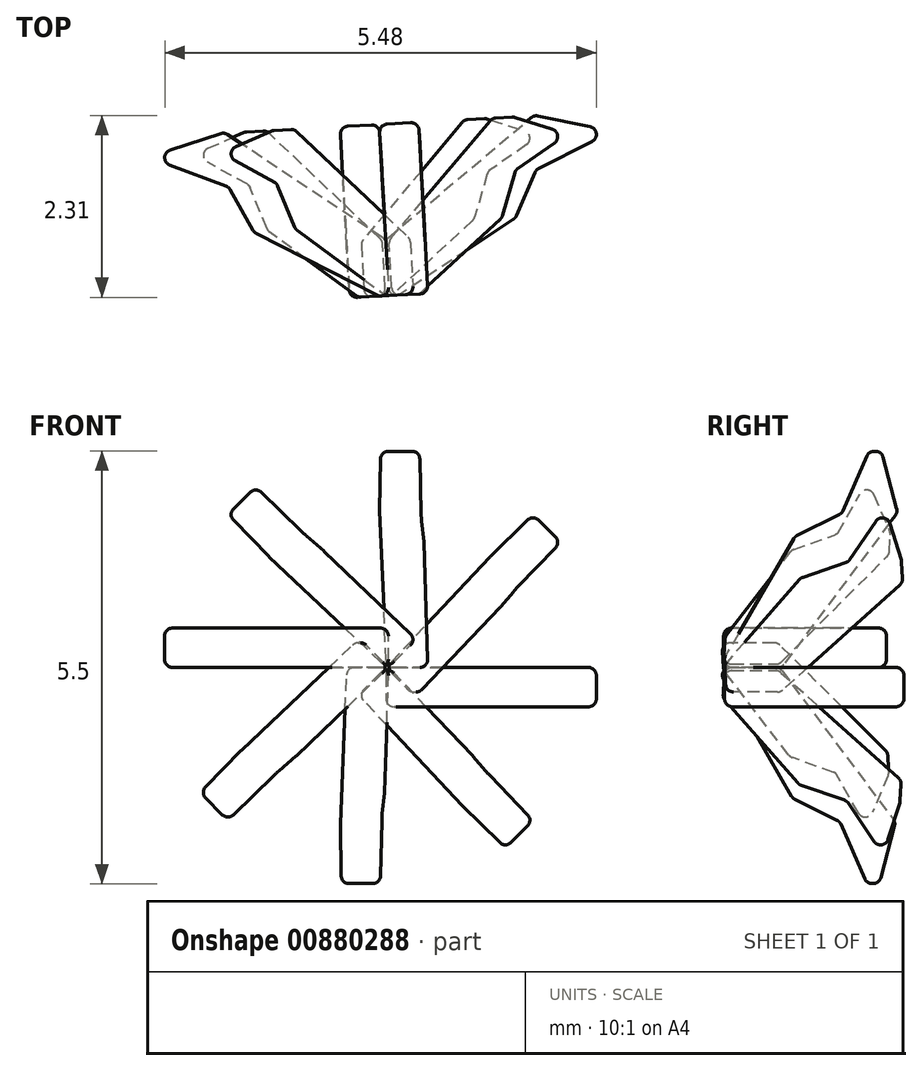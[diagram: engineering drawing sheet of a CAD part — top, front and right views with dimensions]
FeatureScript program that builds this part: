
annotation { "Feature Type Name" : "Feature", "Feature Type Description" : "" }
export const myFeature = defineFeature(function(context is Context, id is Id, definition is map)
    precondition{}
    {
        {
            var Q0;
            Q0=qCreatedBy(makeId("Top.planeOp"),FACE);
            var sketch = newSketch(context, id + "F0", { "sketchPlane" : qUnion([Q0])});
            skLineSegment(sketch, "E0", {"start": v(4.09, 0.78) * mm, "end": v(5.97, 2.37) * mm});
            skLineSegment(sketch, "E1", {"start": v(5.97, 2.37) * mm, "end": v(6.96, 2.16) * mm});
            skLineSegment(sketch, "E2", {"start": v(6.96, 2.16) * mm, "end": v(6, 1.67) * mm});
            skLineSegment(sketch, "E3", {"start": v(6, 1.67) * mm, "end": v(5.73, 1.06) * mm});
            skLineSegment(sketch, "E4", {"start": v(5.73, 1.06) * mm, "end": v(4.13, 0) * mm});
            skLineSegment(sketch, "E5", {"start": v(4.13, 0) * mm, "end": v(4.09, 0.78) * mm});
            skSolve(sketch);
        }
        {
            var Q0;
            Q0=makeQuery(id+"F0.imprint","IMPRINT",FACE,{"disambiguationData":[TD([[makeQuery(id+"F0.imprint","IMPRINT",EDGE,{"derivedFrom":sQuery(id+"F0.wireOp",EDGE,"E0")}),-1.0]])]});
            extrude(context, id + "F1", {"entities" : qUnion([Q0]), "depth" : .5 * mm, "offsetDistance" : 25 * mm});
        }
        {
            var Q0;
            Q0=makeQuery(id+"F1.opExtrude","SWEPT_BODY",BODY,{"disambiguationData":[OSD([sQuery(id+"F0.wireOp",EDGE,"E0"),sQuery(id+"F0.wireOp",EDGE,"E1"),sQuery(id+"F0.wireOp",EDGE,"E2"),sQuery(id+"F0.wireOp",EDGE,"E3"),sQuery(id+"F0.wireOp",EDGE,"E4"),sQuery(id+"F0.wireOp",EDGE,"E5")])]});
            var Q1;
            Q1=makeQuery(id+"F1.opExtrude","CAP_EDGE",EDGE,{"disambiguationData":[OSD([sQuery(id+"F0.wireOp",EDGE,"E5")])],"isStart":false});
            circularPattern(context, id + "F2", {"entities" : qUnion([Q0]), "axis" : qUnion([Q1]), "angle" : 360 * degree, "instanceCount" : 8, "equalSpace" : true});
        }
        {
            var Q0;
            Q0=makeQuery(id+"F2.opPattern","COPY",EDGE,{"derivedFrom":makeQuery(id+"F1.opExtrude","SWEPT_EDGE",EDGE,{"disambiguationData":[OSD([sQuery(id+"F0.wireOp",EDGE,"E0"),sQuery(id+"F0.wireOp",EDGE,"E1")])]}),"instanceName":"4"});
            var Q1;
            Q1=makeQuery(id+"F2.opPattern","COPY",EDGE,{"derivedFrom":makeQuery(id+"F1.opExtrude","CAP_EDGE",EDGE,{"disambiguationData":[OSD([sQuery(id+"F0.wireOp",EDGE,"E0")])],"isStart":false}),"instanceName":"4"});
            var Q2;
            Q2=makeQuery(id+"F2.opPattern","COPY",FACE,{"derivedFrom":makeQuery(id+"F1.opExtrude","SWEPT_FACE",FACE,{"disambiguationData":[OSD([sQuery(id+"F0.wireOp",EDGE,"E0")])]}),"instanceName":"4"});
            var Q3;
            Q3=makeQuery(id+"F2.opPattern","COPY",FACE,{"derivedFrom":makeQuery(id+"F1.opExtrude","CAP_FACE",FACE,{"disambiguationData":[OSD([sQuery(id+"F0.wireOp",EDGE,"E0"),sQuery(id+"F0.wireOp",EDGE,"E1"),sQuery(id+"F0.wireOp",EDGE,"E2"),sQuery(id+"F0.wireOp",EDGE,"E3"),sQuery(id+"F0.wireOp",EDGE,"E4"),sQuery(id+"F0.wireOp",EDGE,"E5")])],"isStart":false}),"instanceName":"4"});
            var Q4;
            Q4=makeQuery(id+"F2.opPattern","COPY",EDGE,{"derivedFrom":makeQuery(id+"F1.opExtrude","CAP_EDGE",EDGE,{"disambiguationData":[OSD([sQuery(id+"F0.wireOp",EDGE,"E0")])],"isStart":true}),"instanceName":"4"});
            var Q5;
            Q5=makeQuery(id+"F2.opPattern","COPY",FACE,{"derivedFrom":makeQuery(id+"F1.opExtrude","CAP_FACE",FACE,{"disambiguationData":[OSD([sQuery(id+"F0.wireOp",EDGE,"E0"),sQuery(id+"F0.wireOp",EDGE,"E1"),sQuery(id+"F0.wireOp",EDGE,"E2"),sQuery(id+"F0.wireOp",EDGE,"E3"),sQuery(id+"F0.wireOp",EDGE,"E4"),sQuery(id+"F0.wireOp",EDGE,"E5")])],"isStart":true}),"instanceName":"4"});
            var Q6;
            Q6=makeQuery(id+"F2.opPattern","COPY",FACE,{"derivedFrom":makeQuery(id+"F1.opExtrude","SWEPT_FACE",FACE,{"disambiguationData":[OSD([sQuery(id+"F0.wireOp",EDGE,"E2")])]}),"instanceName":"4"});
            var Q7;
            Q7=makeQuery(id+"F2.opPattern","COPY",FACE,{"derivedFrom":makeQuery(id+"F1.opExtrude","SWEPT_FACE",FACE,{"disambiguationData":[OSD([sQuery(id+"F0.wireOp",EDGE,"E1")])]}),"instanceName":"4"});
            var Q8;
            Q8=makeQuery(id+"F2.opPattern","COPY",FACE,{"derivedFrom":makeQuery(id+"F1.opExtrude","CAP_FACE",FACE,{"disambiguationData":[OSD([sQuery(id+"F0.wireOp",EDGE,"E0"),sQuery(id+"F0.wireOp",EDGE,"E1"),sQuery(id+"F0.wireOp",EDGE,"E2"),sQuery(id+"F0.wireOp",EDGE,"E3"),sQuery(id+"F0.wireOp",EDGE,"E4"),sQuery(id+"F0.wireOp",EDGE,"E5")])],"isStart":false}),"instanceName":"5"});
            var Q9;
            Q9=makeQuery(id+"F2.opPattern","COPY",EDGE,{"derivedFrom":makeQuery(id+"F1.opExtrude","CAP_EDGE",EDGE,{"disambiguationData":[OSD([sQuery(id+"F0.wireOp",EDGE,"E0")])],"isStart":true}),"instanceName":"5"});
            var Q10;
            Q10=makeQuery(id+"F2.opPattern","COPY",FACE,{"derivedFrom":makeQuery(id+"F1.opExtrude","SWEPT_FACE",FACE,{"disambiguationData":[OSD([sQuery(id+"F0.wireOp",EDGE,"E1")])]}),"instanceName":"5"});
            var Q11;
            Q11=makeQuery(id+"F2.opPattern","COPY",FACE,{"derivedFrom":makeQuery(id+"F1.opExtrude","SWEPT_FACE",FACE,{"disambiguationData":[OSD([sQuery(id+"F0.wireOp",EDGE,"E2")])]}),"instanceName":"5"});
            var Q12;
            Q12=makeQuery(id+"F2.opPattern","COPY",FACE,{"derivedFrom":makeQuery(id+"F1.opExtrude","SWEPT_FACE",FACE,{"disambiguationData":[OSD([sQuery(id+"F0.wireOp",EDGE,"E0")])]}),"instanceName":"5"});
            var Q13;
            Q13=makeQuery(id+"F2.opPattern","COPY",FACE,{"derivedFrom":makeQuery(id+"F1.opExtrude","CAP_FACE",FACE,{"disambiguationData":[OSD([sQuery(id+"F0.wireOp",EDGE,"E0"),sQuery(id+"F0.wireOp",EDGE,"E1"),sQuery(id+"F0.wireOp",EDGE,"E2"),sQuery(id+"F0.wireOp",EDGE,"E3"),sQuery(id+"F0.wireOp",EDGE,"E4"),sQuery(id+"F0.wireOp",EDGE,"E5")])],"isStart":true}),"instanceName":"5"});
            var Q14;
            Q14=makeQuery(id+"F2.opPattern","COPY",FACE,{"derivedFrom":makeQuery(id+"F1.opExtrude","SWEPT_FACE",FACE,{"disambiguationData":[OSD([sQuery(id+"F0.wireOp",EDGE,"E3")])]}),"instanceName":"5"});
            var Q15;
            Q15=makeQuery(id+"F2.opPattern","COPY",FACE,{"derivedFrom":makeQuery(id+"F1.opExtrude","CAP_FACE",FACE,{"disambiguationData":[OSD([sQuery(id+"F0.wireOp",EDGE,"E0"),sQuery(id+"F0.wireOp",EDGE,"E1"),sQuery(id+"F0.wireOp",EDGE,"E2"),sQuery(id+"F0.wireOp",EDGE,"E3"),sQuery(id+"F0.wireOp",EDGE,"E4"),sQuery(id+"F0.wireOp",EDGE,"E5")])],"isStart":false}),"instanceName":"3"});
            var Q16;
            Q16=makeQuery(id+"F2.opPattern","COPY",FACE,{"derivedFrom":makeQuery(id+"F1.opExtrude","SWEPT_FACE",FACE,{"disambiguationData":[OSD([sQuery(id+"F0.wireOp",EDGE,"E2")])]}),"instanceName":"3"});
            var Q17;
            Q17=makeQuery(id+"F2.opPattern","COPY",FACE,{"derivedFrom":makeQuery(id+"F1.opExtrude","SWEPT_FACE",FACE,{"disambiguationData":[OSD([sQuery(id+"F0.wireOp",EDGE,"E0")])]}),"instanceName":"3"});
            var Q18;
            Q18=makeQuery(id+"F2.opPattern","COPY",EDGE,{"derivedFrom":makeQuery(id+"F1.opExtrude","CAP_EDGE",EDGE,{"disambiguationData":[OSD([sQuery(id+"F0.wireOp",EDGE,"E1")])],"isStart":false}),"instanceName":"3"});
            var Q19;
            Q19=makeQuery(id+"F2.opPattern","COPY",FACE,{"derivedFrom":makeQuery(id+"F1.opExtrude","SWEPT_FACE",FACE,{"disambiguationData":[OSD([sQuery(id+"F0.wireOp",EDGE,"E1")])]}),"instanceName":"3"});
            var Q20;
            Q20=makeQuery(id+"F2.opPattern","COPY",FACE,{"derivedFrom":makeQuery(id+"F1.opExtrude","CAP_FACE",FACE,{"disambiguationData":[OSD([sQuery(id+"F0.wireOp",EDGE,"E0"),sQuery(id+"F0.wireOp",EDGE,"E1"),sQuery(id+"F0.wireOp",EDGE,"E2"),sQuery(id+"F0.wireOp",EDGE,"E3"),sQuery(id+"F0.wireOp",EDGE,"E4"),sQuery(id+"F0.wireOp",EDGE,"E5")])],"isStart":true}),"instanceName":"3"});
            var Q21;
            Q21=makeQuery(id+"F2.opPattern","COPY",EDGE,{"derivedFrom":makeQuery(id+"F1.opExtrude","CAP_EDGE",EDGE,{"disambiguationData":[OSD([sQuery(id+"F0.wireOp",EDGE,"E0")])],"isStart":true}),"instanceName":"7"});
            var Q22;
            Q22=makeQuery(id+"F2.opPattern","COPY",EDGE,{"derivedFrom":makeQuery(id+"F1.opExtrude","SWEPT_EDGE",EDGE,{"disambiguationData":[OSD([sQuery(id+"F0.wireOp",EDGE,"E1"),sQuery(id+"F0.wireOp",EDGE,"E2")])]}),"instanceName":"7"});
            var Q23;
            Q23=makeQuery(id+"F2.opPattern","COPY",FACE,{"derivedFrom":makeQuery(id+"F1.opExtrude","CAP_FACE",FACE,{"disambiguationData":[OSD([sQuery(id+"F0.wireOp",EDGE,"E0"),sQuery(id+"F0.wireOp",EDGE,"E1"),sQuery(id+"F0.wireOp",EDGE,"E2"),sQuery(id+"F0.wireOp",EDGE,"E3"),sQuery(id+"F0.wireOp",EDGE,"E4"),sQuery(id+"F0.wireOp",EDGE,"E5")])],"isStart":false}),"instanceName":"7"});
            var Q24;
            Q24=makeQuery(id+"F2.opPattern","COPY",FACE,{"derivedFrom":makeQuery(id+"F1.opExtrude","SWEPT_FACE",FACE,{"disambiguationData":[OSD([sQuery(id+"F0.wireOp",EDGE,"E0")])]}),"instanceName":"7"});
            var Q25;
            Q25=makeQuery(id+"F2.opPattern","COPY",EDGE,{"derivedFrom":makeQuery(id+"F1.opExtrude","CAP_EDGE",EDGE,{"disambiguationData":[OSD([sQuery(id+"F0.wireOp",EDGE,"E0")])],"isStart":false}),"instanceName":"7"});
            var Q26;
            Q26=makeQuery(id+"F2.opPattern","COPY",FACE,{"derivedFrom":makeQuery(id+"F1.opExtrude","SWEPT_FACE",FACE,{"disambiguationData":[OSD([sQuery(id+"F0.wireOp",EDGE,"E1")])]}),"instanceName":"7"});
            var Q27;
            Q27=makeQuery(id+"F2.opPattern","COPY",FACE,{"derivedFrom":makeQuery(id+"F1.opExtrude","CAP_FACE",FACE,{"disambiguationData":[OSD([sQuery(id+"F0.wireOp",EDGE,"E0"),sQuery(id+"F0.wireOp",EDGE,"E1"),sQuery(id+"F0.wireOp",EDGE,"E2"),sQuery(id+"F0.wireOp",EDGE,"E3"),sQuery(id+"F0.wireOp",EDGE,"E4"),sQuery(id+"F0.wireOp",EDGE,"E5")])],"isStart":true}),"instanceName":"7"});
            var Q28;
            Q28=makeQuery(id+"F2.opPattern","COPY",FACE,{"derivedFrom":makeQuery(id+"F1.opExtrude","SWEPT_FACE",FACE,{"disambiguationData":[OSD([sQuery(id+"F0.wireOp",EDGE,"E3")])]}),"instanceName":"7"});
            var Q29;
            Q29=makeQuery(id+"F2.opPattern","COPY",FACE,{"derivedFrom":makeQuery(id+"F1.opExtrude","SWEPT_FACE",FACE,{"disambiguationData":[OSD([sQuery(id+"F0.wireOp",EDGE,"E0")])]}),"instanceName":"6"});
            var Q30;
            Q30=makeQuery(id+"F2.opPattern","COPY",EDGE,{"derivedFrom":makeQuery(id+"F1.opExtrude","SWEPT_EDGE",EDGE,{"disambiguationData":[OSD([sQuery(id+"F0.wireOp",EDGE,"E0"),sQuery(id+"F0.wireOp",EDGE,"E1")])]}),"instanceName":"6"});
            var Q31;
            Q31=makeQuery(id+"F2.opPattern","COPY",FACE,{"derivedFrom":makeQuery(id+"F1.opExtrude","SWEPT_FACE",FACE,{"disambiguationData":[OSD([sQuery(id+"F0.wireOp",EDGE,"E5")])]}),"instanceName":"6"});
            var Q32;
            Q32=makeQuery(id+"F2.opPattern","COPY",FACE,{"derivedFrom":makeQuery(id+"F1.opExtrude","CAP_FACE",FACE,{"disambiguationData":[OSD([sQuery(id+"F0.wireOp",EDGE,"E0"),sQuery(id+"F0.wireOp",EDGE,"E1"),sQuery(id+"F0.wireOp",EDGE,"E2"),sQuery(id+"F0.wireOp",EDGE,"E3"),sQuery(id+"F0.wireOp",EDGE,"E4"),sQuery(id+"F0.wireOp",EDGE,"E5")])],"isStart":true}),"instanceName":"6"});
            var Q33;
            Q33=makeQuery(id+"F2.opPattern","COPY",FACE,{"derivedFrom":makeQuery(id+"F1.opExtrude","CAP_FACE",FACE,{"disambiguationData":[OSD([sQuery(id+"F0.wireOp",EDGE,"E0"),sQuery(id+"F0.wireOp",EDGE,"E1"),sQuery(id+"F0.wireOp",EDGE,"E2"),sQuery(id+"F0.wireOp",EDGE,"E3"),sQuery(id+"F0.wireOp",EDGE,"E4"),sQuery(id+"F0.wireOp",EDGE,"E5")])],"isStart":false}),"instanceName":"6"});
            var Q34;
            Q34=makeQuery(id+"F2.opPattern","COPY",EDGE,{"derivedFrom":makeQuery(id+"F1.opExtrude","CAP_EDGE",EDGE,{"disambiguationData":[OSD([sQuery(id+"F0.wireOp",EDGE,"E0")])],"isStart":false}),"instanceName":"6"});
            var Q35;
            Q35=makeQuery(id+"F2.opPattern","COPY",FACE,{"derivedFrom":makeQuery(id+"F1.opExtrude","SWEPT_FACE",FACE,{"disambiguationData":[OSD([sQuery(id+"F0.wireOp",EDGE,"E1")])]}),"instanceName":"6"});
            var Q36;
            Q36=makeQuery(id+"F1.opExtrude","CAP_FACE",FACE,{"disambiguationData":[OSD([sQuery(id+"F0.wireOp",EDGE,"E0"),sQuery(id+"F0.wireOp",EDGE,"E1"),sQuery(id+"F0.wireOp",EDGE,"E2"),sQuery(id+"F0.wireOp",EDGE,"E3"),sQuery(id+"F0.wireOp",EDGE,"E4"),sQuery(id+"F0.wireOp",EDGE,"E5")])],"isStart":true});
            var Q37;
            Q37=makeQuery(id+"F1.opExtrude","CAP_EDGE",EDGE,{"disambiguationData":[OSD([sQuery(id+"F0.wireOp",EDGE,"E1")])],"isStart":false});
            var Q38;
            Q38=makeQuery(id+"F1.opExtrude","SWEPT_EDGE",EDGE,{"disambiguationData":[OSD([sQuery(id+"F0.wireOp",EDGE,"E0"),sQuery(id+"F0.wireOp",EDGE,"E1")])]});
            var Q39;
            Q39=makeQuery(id+"F1.opExtrude","SWEPT_FACE",FACE,{"disambiguationData":[OSD([sQuery(id+"F0.wireOp",EDGE,"E0")])]});
            var Q40;
            Q40=makeQuery(id+"F1.opExtrude","SWEPT_FACE",FACE,{"disambiguationData":[OSD([sQuery(id+"F0.wireOp",EDGE,"E1")])]});
            var Q41;
            Q41=makeQuery(id+"F2.opPattern","COPY",FACE,{"derivedFrom":makeQuery(id+"F1.opExtrude","CAP_FACE",FACE,{"disambiguationData":[OSD([sQuery(id+"F0.wireOp",EDGE,"E0"),sQuery(id+"F0.wireOp",EDGE,"E1"),sQuery(id+"F0.wireOp",EDGE,"E2"),sQuery(id+"F0.wireOp",EDGE,"E3"),sQuery(id+"F0.wireOp",EDGE,"E4"),sQuery(id+"F0.wireOp",EDGE,"E5")])],"isStart":false}),"instanceName":"2"});
            var Q42;
            Q42=makeQuery(id+"F2.opPattern","COPY",FACE,{"derivedFrom":makeQuery(id+"F1.opExtrude","SWEPT_FACE",FACE,{"disambiguationData":[OSD([sQuery(id+"F0.wireOp",EDGE,"E1")])]}),"instanceName":"2"});
            var Q43;
            Q43=makeQuery(id+"F2.opPattern","COPY",FACE,{"derivedFrom":makeQuery(id+"F1.opExtrude","SWEPT_FACE",FACE,{"disambiguationData":[OSD([sQuery(id+"F0.wireOp",EDGE,"E0")])]}),"instanceName":"2"});
            var Q44;
            Q44=makeQuery(id+"F2.opPattern","COPY",FACE,{"derivedFrom":makeQuery(id+"F1.opExtrude","CAP_FACE",FACE,{"disambiguationData":[OSD([sQuery(id+"F0.wireOp",EDGE,"E0"),sQuery(id+"F0.wireOp",EDGE,"E1"),sQuery(id+"F0.wireOp",EDGE,"E2"),sQuery(id+"F0.wireOp",EDGE,"E3"),sQuery(id+"F0.wireOp",EDGE,"E4"),sQuery(id+"F0.wireOp",EDGE,"E5")])],"isStart":true}),"instanceName":"2"});
            var Q45;
            Q45=makeQuery(id+"F2.opPattern","COPY",EDGE,{"derivedFrom":makeQuery(id+"F1.opExtrude","CAP_EDGE",EDGE,{"disambiguationData":[OSD([sQuery(id+"F0.wireOp",EDGE,"E0")])],"isStart":true}),"instanceName":"1"});
            var Q46;
            Q46=makeQuery(id+"F2.opPattern","COPY",FACE,{"derivedFrom":makeQuery(id+"F1.opExtrude","CAP_FACE",FACE,{"disambiguationData":[OSD([sQuery(id+"F0.wireOp",EDGE,"E0"),sQuery(id+"F0.wireOp",EDGE,"E1"),sQuery(id+"F0.wireOp",EDGE,"E2"),sQuery(id+"F0.wireOp",EDGE,"E3"),sQuery(id+"F0.wireOp",EDGE,"E4"),sQuery(id+"F0.wireOp",EDGE,"E5")])],"isStart":true}),"instanceName":"1"});
            var Q47;
            Q47=makeQuery(id+"F2.opPattern","COPY",EDGE,{"derivedFrom":makeQuery(id+"F1.opExtrude","CAP_EDGE",EDGE,{"disambiguationData":[OSD([sQuery(id+"F0.wireOp",EDGE,"E1")])],"isStart":true}),"instanceName":"1"});
            var Q48;
            Q48=makeQuery(id+"F2.opPattern","COPY",FACE,{"derivedFrom":makeQuery(id+"F1.opExtrude","SWEPT_FACE",FACE,{"disambiguationData":[OSD([sQuery(id+"F0.wireOp",EDGE,"E0")])]}),"instanceName":"1"});
            var Q49;
            Q49=makeQuery(id+"F2.opPattern","COPY",EDGE,{"derivedFrom":makeQuery(id+"F1.opExtrude","CAP_EDGE",EDGE,{"disambiguationData":[OSD([sQuery(id+"F0.wireOp",EDGE,"E0")])],"isStart":false}),"instanceName":"1"});
            var Q50;
            Q50=makeQuery(id+"F2.opPattern","COPY",EDGE,{"derivedFrom":makeQuery(id+"F1.opExtrude","CAP_EDGE",EDGE,{"disambiguationData":[OSD([sQuery(id+"F0.wireOp",EDGE,"E1")])],"isStart":false}),"instanceName":"1"});
            var Q51;
            Q51=makeQuery(id+"F2.opPattern","COPY",FACE,{"derivedFrom":makeQuery(id+"F1.opExtrude","SWEPT_FACE",FACE,{"disambiguationData":[OSD([sQuery(id+"F0.wireOp",EDGE,"E1")])]}),"instanceName":"1"});
            var Q52;
            Q52=makeQuery(id+"F2.opPattern","COPY",EDGE,{"derivedFrom":makeQuery(id+"F1.opExtrude","SWEPT_EDGE",EDGE,{"disambiguationData":[OSD([sQuery(id+"F0.wireOp",EDGE,"E2"),sQuery(id+"F0.wireOp",EDGE,"E3")])]}),"instanceName":"4"});
            var Q53;
            Q53=makeQuery(id+"F2.opPattern","COPY",EDGE,{"derivedFrom":makeQuery(id+"F1.opExtrude","SWEPT_EDGE",EDGE,{"disambiguationData":[OSD([sQuery(id+"F0.wireOp",EDGE,"E1"),sQuery(id+"F0.wireOp",EDGE,"E2")])]}),"instanceName":"4"});
            var Q54;
            Q54=makeQuery(id+"F2.opPattern","COPY",FACE,{"derivedFrom":makeQuery(id+"F1.opExtrude","SWEPT_FACE",FACE,{"disambiguationData":[OSD([sQuery(id+"F0.wireOp",EDGE,"E3")])]}),"instanceName":"4"});
            var Q55;
            Q55=makeQuery(id+"F2.opPattern","COPY",EDGE,{"derivedFrom":makeQuery(id+"F1.opExtrude","CAP_EDGE",EDGE,{"disambiguationData":[OSD([sQuery(id+"F0.wireOp",EDGE,"E3")])],"isStart":false}),"instanceName":"4"});
            var Q56;
            Q56=makeQuery(id+"F2.opPattern","COPY",EDGE,{"derivedFrom":makeQuery(id+"F1.opExtrude","CAP_EDGE",EDGE,{"disambiguationData":[OSD([sQuery(id+"F0.wireOp",EDGE,"E1")])],"isStart":false}),"instanceName":"4"});
            var Q57;
            Q57=makeQuery(id+"F2.opPattern","COPY",EDGE,{"derivedFrom":makeQuery(id+"F1.opExtrude","CAP_EDGE",EDGE,{"disambiguationData":[OSD([sQuery(id+"F0.wireOp",EDGE,"E2")])],"isStart":false}),"instanceName":"4"});
            var Q58;
            Q58=makeQuery(id+"F2.opPattern","COPY",FACE,{"derivedFrom":makeQuery(id+"F1.opExtrude","SWEPT_FACE",FACE,{"disambiguationData":[OSD([sQuery(id+"F0.wireOp",EDGE,"E4")])]}),"instanceName":"4"});
            var Q59;
            Q59=makeQuery(id+"F2.opPattern","COPY",EDGE,{"derivedFrom":makeQuery(id+"F1.opExtrude","CAP_EDGE",EDGE,{"disambiguationData":[OSD([sQuery(id+"F0.wireOp",EDGE,"E1")])],"isStart":true}),"instanceName":"4"});
            var Q60;
            Q60=makeQuery(id+"F2.opPattern","COPY",EDGE,{"derivedFrom":makeQuery(id+"F1.opExtrude","CAP_EDGE",EDGE,{"disambiguationData":[OSD([sQuery(id+"F0.wireOp",EDGE,"E2")])],"isStart":true}),"instanceName":"4"});
            var Q61;
            Q61=makeQuery(id+"F2.opPattern","COPY",EDGE,{"derivedFrom":makeQuery(id+"F1.opExtrude","SWEPT_EDGE",EDGE,{"disambiguationData":[OSD([sQuery(id+"F0.wireOp",EDGE,"E2"),sQuery(id+"F0.wireOp",EDGE,"E3")])]}),"instanceName":"5"});
            var Q62;
            Q62=makeQuery(id+"F2.opPattern","COPY",EDGE,{"derivedFrom":makeQuery(id+"F1.opExtrude","CAP_EDGE",EDGE,{"disambiguationData":[OSD([sQuery(id+"F0.wireOp",EDGE,"E1")])],"isStart":true}),"instanceName":"5"});
            var Q63;
            Q63=makeQuery(id+"F2.opPattern","COPY",EDGE,{"derivedFrom":makeQuery(id+"F1.opExtrude","SWEPT_EDGE",EDGE,{"disambiguationData":[OSD([sQuery(id+"F0.wireOp",EDGE,"E0"),sQuery(id+"F0.wireOp",EDGE,"E1")])]}),"instanceName":"5"});
            var Q64;
            Q64=makeQuery(id+"F2.opPattern","COPY",EDGE,{"derivedFrom":makeQuery(id+"F1.opExtrude","CAP_EDGE",EDGE,{"disambiguationData":[OSD([sQuery(id+"F0.wireOp",EDGE,"E2")])],"isStart":false}),"instanceName":"5"});
            var Q65;
            Q65=makeQuery(id+"F2.opPattern","COPY",EDGE,{"derivedFrom":makeQuery(id+"F1.opExtrude","CAP_EDGE",EDGE,{"disambiguationData":[OSD([sQuery(id+"F0.wireOp",EDGE,"E3")])],"isStart":false}),"instanceName":"5"});
            var Q66;
            Q66=makeQuery(id+"F2.opPattern","COPY",EDGE,{"derivedFrom":makeQuery(id+"F1.opExtrude","SWEPT_EDGE",EDGE,{"disambiguationData":[OSD([sQuery(id+"F0.wireOp",EDGE,"E3"),sQuery(id+"F0.wireOp",EDGE,"E4")])]}),"instanceName":"5"});
            var Q67;
            Q67=makeQuery(id+"F2.opPattern","COPY",FACE,{"derivedFrom":makeQuery(id+"F1.opExtrude","SWEPT_FACE",FACE,{"disambiguationData":[OSD([sQuery(id+"F0.wireOp",EDGE,"E4")])]}),"instanceName":"5"});
            var Q68;
            Q68=makeQuery(id+"F2.opPattern","COPY",EDGE,{"derivedFrom":makeQuery(id+"F1.opExtrude","CAP_EDGE",EDGE,{"disambiguationData":[OSD([sQuery(id+"F0.wireOp",EDGE,"E3")])],"isStart":true}),"instanceName":"5"});
            var Q69;
            Q69=makeQuery(id+"F2.opPattern","COPY",EDGE,{"derivedFrom":makeQuery(id+"F1.opExtrude","SWEPT_EDGE",EDGE,{"disambiguationData":[OSD([sQuery(id+"F0.wireOp",EDGE,"E1"),sQuery(id+"F0.wireOp",EDGE,"E2")])]}),"instanceName":"5"});
            var Q70;
            Q70=makeQuery(id+"F2.opPattern","COPY",EDGE,{"derivedFrom":makeQuery(id+"F1.opExtrude","CAP_EDGE",EDGE,{"disambiguationData":[OSD([sQuery(id+"F0.wireOp",EDGE,"E0")])],"isStart":false}),"instanceName":"5"});
            var Q71;
            Q71=makeQuery(id+"F2.opPattern","COPY",EDGE,{"derivedFrom":makeQuery(id+"F1.opExtrude","CAP_EDGE",EDGE,{"disambiguationData":[OSD([sQuery(id+"F0.wireOp",EDGE,"E1")])],"isStart":false}),"instanceName":"5"});
            var Q72;
            Q72=makeQuery(id+"F2.opPattern","COPY",EDGE,{"derivedFrom":makeQuery(id+"F1.opExtrude","CAP_EDGE",EDGE,{"disambiguationData":[OSD([sQuery(id+"F0.wireOp",EDGE,"E2")])],"isStart":true}),"instanceName":"5"});
            var Q73;
            Q73=makeQuery(id+"F2.opPattern","COPY",EDGE,{"derivedFrom":makeQuery(id+"F1.opExtrude","CAP_EDGE",EDGE,{"disambiguationData":[OSD([sQuery(id+"F0.wireOp",EDGE,"E1")])],"isStart":true}),"instanceName":"3"});
            var Q74;
            Q74=makeQuery(id+"F2.opPattern","COPY",EDGE,{"derivedFrom":makeQuery(id+"F1.opExtrude","SWEPT_EDGE",EDGE,{"disambiguationData":[OSD([sQuery(id+"F0.wireOp",EDGE,"E3"),sQuery(id+"F0.wireOp",EDGE,"E4")])]}),"instanceName":"3"});
            var Q75;
            Q75=makeQuery(id+"F2.opPattern","COPY",FACE,{"derivedFrom":makeQuery(id+"F1.opExtrude","SWEPT_FACE",FACE,{"disambiguationData":[OSD([sQuery(id+"F0.wireOp",EDGE,"E3")])]}),"instanceName":"3"});
            var Q76;
            Q76=makeQuery(id+"F2.opPattern","COPY",EDGE,{"derivedFrom":makeQuery(id+"F1.opExtrude","CAP_EDGE",EDGE,{"disambiguationData":[OSD([sQuery(id+"F0.wireOp",EDGE,"E2")])],"isStart":true}),"instanceName":"3"});
            var Q77;
            Q77=makeQuery(id+"F2.opPattern","COPY",EDGE,{"derivedFrom":makeQuery(id+"F1.opExtrude","CAP_EDGE",EDGE,{"disambiguationData":[OSD([sQuery(id+"F0.wireOp",EDGE,"E0")])],"isStart":true}),"instanceName":"3"});
            var Q78;
            Q78=makeQuery(id+"F2.opPattern","COPY",EDGE,{"derivedFrom":makeQuery(id+"F1.opExtrude","CAP_EDGE",EDGE,{"disambiguationData":[OSD([sQuery(id+"F0.wireOp",EDGE,"E0")])],"isStart":false}),"instanceName":"3"});
            var Q79;
            Q79=makeQuery(id+"F2.opPattern","COPY",EDGE,{"derivedFrom":makeQuery(id+"F1.opExtrude","SWEPT_EDGE",EDGE,{"disambiguationData":[OSD([sQuery(id+"F0.wireOp",EDGE,"E1"),sQuery(id+"F0.wireOp",EDGE,"E2")])]}),"instanceName":"3"});
            var Q80;
            Q80=makeQuery(id+"F2.opPattern","COPY",EDGE,{"derivedFrom":makeQuery(id+"F1.opExtrude","SWEPT_EDGE",EDGE,{"disambiguationData":[OSD([sQuery(id+"F0.wireOp",EDGE,"E2"),sQuery(id+"F0.wireOp",EDGE,"E3")])]}),"instanceName":"3"});
            var Q81;
            Q81=makeQuery(id+"F2.opPattern","COPY",EDGE,{"derivedFrom":makeQuery(id+"F1.opExtrude","CAP_EDGE",EDGE,{"disambiguationData":[OSD([sQuery(id+"F0.wireOp",EDGE,"E2")])],"isStart":false}),"instanceName":"3"});
            var Q82;
            Q82=makeQuery(id+"F2.opPattern","COPY",FACE,{"derivedFrom":makeQuery(id+"F1.opExtrude","SWEPT_FACE",FACE,{"disambiguationData":[OSD([sQuery(id+"F0.wireOp",EDGE,"E4")])]}),"instanceName":"3"});
            var Q83;
            Q83=makeQuery(id+"F2.opPattern","COPY",EDGE,{"derivedFrom":makeQuery(id+"F1.opExtrude","SWEPT_EDGE",EDGE,{"disambiguationData":[OSD([sQuery(id+"F0.wireOp",EDGE,"E0"),sQuery(id+"F0.wireOp",EDGE,"E1")])]}),"instanceName":"3"});
            var Q84;
            Q84=makeQuery(id+"F2.opPattern","COPY",EDGE,{"derivedFrom":makeQuery(id+"F1.opExtrude","CAP_EDGE",EDGE,{"disambiguationData":[OSD([sQuery(id+"F0.wireOp",EDGE,"E3")])],"isStart":true}),"instanceName":"7"});
            var Q85;
            Q85=makeQuery(id+"F2.opPattern","COPY",FACE,{"derivedFrom":makeQuery(id+"F1.opExtrude","SWEPT_FACE",FACE,{"disambiguationData":[OSD([sQuery(id+"F0.wireOp",EDGE,"E4")])]}),"instanceName":"7"});
            var Q86;
            Q86=makeQuery(id+"F2.opPattern","COPY",EDGE,{"derivedFrom":makeQuery(id+"F1.opExtrude","CAP_EDGE",EDGE,{"disambiguationData":[OSD([sQuery(id+"F0.wireOp",EDGE,"E3")])],"isStart":false}),"instanceName":"7"});
            var Q87;
            Q87=makeQuery(id+"F2.opPattern","COPY",EDGE,{"derivedFrom":makeQuery(id+"F1.opExtrude","SWEPT_EDGE",EDGE,{"disambiguationData":[OSD([sQuery(id+"F0.wireOp",EDGE,"E2"),sQuery(id+"F0.wireOp",EDGE,"E3")])]}),"instanceName":"7"});
            var Q88;
            Q88=makeQuery(id+"F2.opPattern","COPY",EDGE,{"derivedFrom":makeQuery(id+"F1.opExtrude","CAP_EDGE",EDGE,{"disambiguationData":[OSD([sQuery(id+"F0.wireOp",EDGE,"E1")])],"isStart":true}),"instanceName":"7"});
            var Q89;
            Q89=makeQuery(id+"F2.opPattern","COPY",EDGE,{"derivedFrom":makeQuery(id+"F1.opExtrude","CAP_EDGE",EDGE,{"disambiguationData":[OSD([sQuery(id+"F0.wireOp",EDGE,"E1")])],"isStart":false}),"instanceName":"7"});
            var Q90;
            Q90=makeQuery(id+"F2.opPattern","COPY",FACE,{"derivedFrom":makeQuery(id+"F1.opExtrude","SWEPT_FACE",FACE,{"disambiguationData":[OSD([sQuery(id+"F0.wireOp",EDGE,"E2")])]}),"instanceName":"7"});
            var Q91;
            Q91=makeQuery(id+"F2.opPattern","COPY",EDGE,{"derivedFrom":makeQuery(id+"F1.opExtrude","SWEPT_EDGE",EDGE,{"disambiguationData":[OSD([sQuery(id+"F0.wireOp",EDGE,"E0"),sQuery(id+"F0.wireOp",EDGE,"E1")])]}),"instanceName":"7"});
            var Q92;
            Q92=makeQuery(id+"F2.opPattern","COPY",EDGE,{"derivedFrom":makeQuery(id+"F1.opExtrude","SWEPT_EDGE",EDGE,{"disambiguationData":[OSD([sQuery(id+"F0.wireOp",EDGE,"E3"),sQuery(id+"F0.wireOp",EDGE,"E4")])]}),"instanceName":"7"});
            var Q93;
            Q93=makeQuery(id+"F2.opPattern","COPY",EDGE,{"derivedFrom":makeQuery(id+"F1.opExtrude","CAP_EDGE",EDGE,{"disambiguationData":[OSD([sQuery(id+"F0.wireOp",EDGE,"E2")])],"isStart":true}),"instanceName":"7"});
            var Q94;
            Q94=makeQuery(id+"F2.opPattern","COPY",EDGE,{"derivedFrom":makeQuery(id+"F1.opExtrude","CAP_EDGE",EDGE,{"disambiguationData":[OSD([sQuery(id+"F0.wireOp",EDGE,"E4")])],"isStart":false}),"instanceName":"7"});
            var Q95;
            Q95=makeQuery(id+"F2.opPattern","COPY",EDGE,{"derivedFrom":makeQuery(id+"F1.opExtrude","CAP_EDGE",EDGE,{"disambiguationData":[OSD([sQuery(id+"F0.wireOp",EDGE,"E4")])],"isStart":true}),"instanceName":"7"});
            var Q96;
            Q96=makeQuery(id+"F2.opPattern","COPY",EDGE,{"derivedFrom":makeQuery(id+"F1.opExtrude","SWEPT_EDGE",EDGE,{"disambiguationData":[OSD([sQuery(id+"F0.wireOp",EDGE,"E3"),sQuery(id+"F0.wireOp",EDGE,"E4")])]}),"instanceName":"6"});
            var Q97;
            Q97=makeQuery(id+"F2.opPattern","COPY",FACE,{"derivedFrom":makeQuery(id+"F1.opExtrude","SWEPT_FACE",FACE,{"disambiguationData":[OSD([sQuery(id+"F0.wireOp",EDGE,"E3")])]}),"instanceName":"6"});
            var Q98;
            Q98=makeQuery(id+"F2.opPattern","COPY",FACE,{"derivedFrom":makeQuery(id+"F1.opExtrude","SWEPT_FACE",FACE,{"disambiguationData":[OSD([sQuery(id+"F0.wireOp",EDGE,"E4")])]}),"instanceName":"6"});
            var Q99;
            Q99=makeQuery(id+"F2.opPattern","COPY",EDGE,{"derivedFrom":makeQuery(id+"F1.opExtrude","CAP_EDGE",EDGE,{"disambiguationData":[OSD([sQuery(id+"F0.wireOp",EDGE,"E0")])],"isStart":true}),"instanceName":"6"});
            var Q100;
            Q100=makeQuery(id+"F2.opPattern","COPY",EDGE,{"derivedFrom":makeQuery(id+"F1.opExtrude","SWEPT_EDGE",EDGE,{"disambiguationData":[OSD([sQuery(id+"F0.wireOp",EDGE,"E1"),sQuery(id+"F0.wireOp",EDGE,"E2")])]}),"instanceName":"6"});
            var Q101;
            Q101=makeQuery(id+"F2.opPattern","COPY",EDGE,{"derivedFrom":makeQuery(id+"F1.opExtrude","CAP_EDGE",EDGE,{"disambiguationData":[OSD([sQuery(id+"F0.wireOp",EDGE,"E1")])],"isStart":false}),"instanceName":"6"});
            var Q102;
            Q102=makeQuery(id+"F2.opPattern","COPY",EDGE,{"derivedFrom":makeQuery(id+"F1.opExtrude","CAP_EDGE",EDGE,{"disambiguationData":[OSD([sQuery(id+"F0.wireOp",EDGE,"E1")])],"isStart":true}),"instanceName":"6"});
            var Q103;
            Q103=makeQuery(id+"F2.opPattern","COPY",EDGE,{"derivedFrom":makeQuery(id+"F1.opExtrude","SWEPT_EDGE",EDGE,{"disambiguationData":[OSD([sQuery(id+"F0.wireOp",EDGE,"E2"),sQuery(id+"F0.wireOp",EDGE,"E3")])]}),"instanceName":"6"});
            var Q104;
            Q104=makeQuery(id+"F2.opPattern","COPY",FACE,{"derivedFrom":makeQuery(id+"F1.opExtrude","SWEPT_FACE",FACE,{"disambiguationData":[OSD([sQuery(id+"F0.wireOp",EDGE,"E2")])]}),"instanceName":"6"});
            var Q105;
            Q105=makeQuery(id+"F1.opExtrude","CAP_EDGE",EDGE,{"disambiguationData":[OSD([sQuery(id+"F0.wireOp",EDGE,"E0")])],"isStart":true});
            var Q106;
            Q106=makeQuery(id+"F1.opExtrude","SWEPT_FACE",FACE,{"disambiguationData":[OSD([sQuery(id+"F0.wireOp",EDGE,"E2")])]});
            var Q107;
            Q107=makeQuery(id+"F1.opExtrude","SWEPT_FACE",FACE,{"disambiguationData":[OSD([sQuery(id+"F0.wireOp",EDGE,"E4")])]});
            var Q108;
            Q108=makeQuery(id+"F1.opExtrude","SWEPT_EDGE",EDGE,{"disambiguationData":[OSD([sQuery(id+"F0.wireOp",EDGE,"E2"),sQuery(id+"F0.wireOp",EDGE,"E3")])]});
            var Q109;
            Q109=makeQuery(id+"F1.opExtrude","SWEPT_FACE",FACE,{"disambiguationData":[OSD([sQuery(id+"F0.wireOp",EDGE,"E3")])]});
            var Q110;
            Q110=makeQuery(id+"F1.opExtrude","SWEPT_EDGE",EDGE,{"disambiguationData":[OSD([sQuery(id+"F0.wireOp",EDGE,"E3"),sQuery(id+"F0.wireOp",EDGE,"E4")])]});
            var Q111;
            Q111=makeQuery(id+"F1.opExtrude","SWEPT_EDGE",EDGE,{"disambiguationData":[OSD([sQuery(id+"F0.wireOp",EDGE,"E1"),sQuery(id+"F0.wireOp",EDGE,"E2")])]});
            var Q112;
            Q112=makeQuery(id+"F1.opExtrude","CAP_EDGE",EDGE,{"disambiguationData":[OSD([sQuery(id+"F0.wireOp",EDGE,"E0")])],"isStart":false});
            var Q113;
            Q113=makeQuery(id+"F1.opExtrude","CAP_FACE",FACE,{"disambiguationData":[OSD([sQuery(id+"F0.wireOp",EDGE,"E0"),sQuery(id+"F0.wireOp",EDGE,"E1"),sQuery(id+"F0.wireOp",EDGE,"E2"),sQuery(id+"F0.wireOp",EDGE,"E3"),sQuery(id+"F0.wireOp",EDGE,"E4"),sQuery(id+"F0.wireOp",EDGE,"E5")])],"isStart":false});
            var Q114;
            Q114=makeQuery(id+"F1.opExtrude","CAP_EDGE",EDGE,{"disambiguationData":[OSD([sQuery(id+"F0.wireOp",EDGE,"E1")])],"isStart":true});
            var Q115;
            Q115=makeQuery(id+"F2.opPattern","COPY",EDGE,{"derivedFrom":makeQuery(id+"F1.opExtrude","CAP_EDGE",EDGE,{"disambiguationData":[OSD([sQuery(id+"F0.wireOp",EDGE,"E0")])],"isStart":true}),"instanceName":"2"});
            var Q116;
            Q116=makeQuery(id+"F2.opPattern","COPY",FACE,{"derivedFrom":makeQuery(id+"F1.opExtrude","SWEPT_FACE",FACE,{"disambiguationData":[OSD([sQuery(id+"F0.wireOp",EDGE,"E5")])]}),"instanceName":"2"});
            var Q117;
            Q117=makeQuery(id+"F2.opPattern","COPY",EDGE,{"derivedFrom":makeQuery(id+"F1.opExtrude","SWEPT_EDGE",EDGE,{"disambiguationData":[OSD([sQuery(id+"F0.wireOp",EDGE,"E2"),sQuery(id+"F0.wireOp",EDGE,"E3")])]}),"instanceName":"2"});
            var Q118;
            Q118=makeQuery(id+"F2.opPattern","COPY",FACE,{"derivedFrom":makeQuery(id+"F1.opExtrude","SWEPT_FACE",FACE,{"disambiguationData":[OSD([sQuery(id+"F0.wireOp",EDGE,"E2")])]}),"instanceName":"2"});
            var Q119;
            Q119=makeQuery(id+"F2.opPattern","COPY",EDGE,{"derivedFrom":makeQuery(id+"F1.opExtrude","CAP_EDGE",EDGE,{"disambiguationData":[OSD([sQuery(id+"F0.wireOp",EDGE,"E1")])],"isStart":true}),"instanceName":"2"});
            var Q120;
            Q120=makeQuery(id+"F2.opPattern","COPY",EDGE,{"derivedFrom":makeQuery(id+"F1.opExtrude","CAP_EDGE",EDGE,{"disambiguationData":[OSD([sQuery(id+"F0.wireOp",EDGE,"E1")])],"isStart":false}),"instanceName":"2"});
            var Q121;
            Q121=makeQuery(id+"F2.opPattern","COPY",EDGE,{"derivedFrom":makeQuery(id+"F1.opExtrude","CAP_EDGE",EDGE,{"disambiguationData":[OSD([sQuery(id+"F0.wireOp",EDGE,"E0")])],"isStart":false}),"instanceName":"2"});
            var Q122;
            Q122=makeQuery(id+"F2.opPattern","COPY",FACE,{"derivedFrom":makeQuery(id+"F1.opExtrude","SWEPT_FACE",FACE,{"disambiguationData":[OSD([sQuery(id+"F0.wireOp",EDGE,"E4")])]}),"instanceName":"2"});
            var Q123;
            Q123=makeQuery(id+"F2.opPattern","COPY",EDGE,{"derivedFrom":makeQuery(id+"F1.opExtrude","SWEPT_EDGE",EDGE,{"disambiguationData":[OSD([sQuery(id+"F0.wireOp",EDGE,"E1"),sQuery(id+"F0.wireOp",EDGE,"E2")])]}),"instanceName":"2"});
            var Q124;
            Q124=makeQuery(id+"F2.opPattern","COPY",EDGE,{"derivedFrom":makeQuery(id+"F1.opExtrude","SWEPT_EDGE",EDGE,{"disambiguationData":[OSD([sQuery(id+"F0.wireOp",EDGE,"E0"),sQuery(id+"F0.wireOp",EDGE,"E1")])]}),"instanceName":"2"});
            var Q125;
            Q125=makeQuery(id+"F2.opPattern","COPY",FACE,{"derivedFrom":makeQuery(id+"F1.opExtrude","SWEPT_FACE",FACE,{"disambiguationData":[OSD([sQuery(id+"F0.wireOp",EDGE,"E4")])]}),"instanceName":"1"});
            var Q126;
            Q126=makeQuery(id+"F2.opPattern","COPY",EDGE,{"derivedFrom":makeQuery(id+"F1.opExtrude","SWEPT_EDGE",EDGE,{"disambiguationData":[OSD([sQuery(id+"F0.wireOp",EDGE,"E2"),sQuery(id+"F0.wireOp",EDGE,"E3")])]}),"instanceName":"1"});
            var Q127;
            Q127=makeQuery(id+"F2.opPattern","COPY",EDGE,{"derivedFrom":makeQuery(id+"F1.opExtrude","SWEPT_EDGE",EDGE,{"disambiguationData":[OSD([sQuery(id+"F0.wireOp",EDGE,"E0"),sQuery(id+"F0.wireOp",EDGE,"E5")])]}),"instanceName":"1"});
            var Q128;
            Q128=makeQuery(id+"F2.opPattern","COPY",EDGE,{"derivedFrom":makeQuery(id+"F1.opExtrude","SWEPT_EDGE",EDGE,{"disambiguationData":[OSD([sQuery(id+"F0.wireOp",EDGE,"E0"),sQuery(id+"F0.wireOp",EDGE,"E1")])]}),"instanceName":"1"});
            var Q129;
            Q129=makeQuery(id+"F2.opPattern","COPY",EDGE,{"derivedFrom":makeQuery(id+"F1.opExtrude","SWEPT_EDGE",EDGE,{"disambiguationData":[OSD([sQuery(id+"F0.wireOp",EDGE,"E1"),sQuery(id+"F0.wireOp",EDGE,"E2")])]}),"instanceName":"1"});
            var Q130;
            Q130=makeQuery(id+"F2.opPattern","COPY",FACE,{"derivedFrom":makeQuery(id+"F1.opExtrude","SWEPT_FACE",FACE,{"disambiguationData":[OSD([sQuery(id+"F0.wireOp",EDGE,"E2")])]}),"instanceName":"1"});
            var Q131;
            Q131=makeQuery(id+"F2.opPattern","COPY",FACE,{"derivedFrom":makeQuery(id+"F1.opExtrude","SWEPT_FACE",FACE,{"disambiguationData":[OSD([sQuery(id+"F0.wireOp",EDGE,"E3")])]}),"instanceName":"1"});
            var Q132;
            Q132=makeQuery(id+"F2.opPattern","COPY",EDGE,{"derivedFrom":makeQuery(id+"F1.opExtrude","SWEPT_EDGE",EDGE,{"disambiguationData":[OSD([sQuery(id+"F0.wireOp",EDGE,"E3"),sQuery(id+"F0.wireOp",EDGE,"E4")])]}),"instanceName":"1"});
            var Q133;
            Q133=makeQuery(id+"F2.opPattern","COPY",FACE,{"derivedFrom":makeQuery(id+"F1.opExtrude","SWEPT_FACE",FACE,{"disambiguationData":[OSD([sQuery(id+"F0.wireOp",EDGE,"E5")])]}),"instanceName":"1"});
            var Q134;
            Q134=makeQuery(id+"F2.opPattern","COPY",FACE,{"derivedFrom":makeQuery(id+"F1.opExtrude","CAP_FACE",FACE,{"disambiguationData":[OSD([sQuery(id+"F0.wireOp",EDGE,"E0"),sQuery(id+"F0.wireOp",EDGE,"E1"),sQuery(id+"F0.wireOp",EDGE,"E2"),sQuery(id+"F0.wireOp",EDGE,"E3"),sQuery(id+"F0.wireOp",EDGE,"E4"),sQuery(id+"F0.wireOp",EDGE,"E5")])],"isStart":false}),"instanceName":"1"});
            var Q135;
            Q135=makeQuery(id+"F2.opPattern","COPY",FACE,{"derivedFrom":makeQuery(id+"F1.opExtrude","SWEPT_FACE",FACE,{"disambiguationData":[OSD([sQuery(id+"F0.wireOp",EDGE,"E5")])]}),"instanceName":"4"});
            var Q136;
            Q136=makeQuery(id+"F2.opPattern","COPY",EDGE,{"derivedFrom":makeQuery(id+"F1.opExtrude","SWEPT_EDGE",EDGE,{"disambiguationData":[OSD([sQuery(id+"F0.wireOp",EDGE,"E0"),sQuery(id+"F0.wireOp",EDGE,"E5")])]}),"instanceName":"4"});
            var Q137;
            Q137=makeQuery(id+"F2.opPattern","COPY",EDGE,{"derivedFrom":makeQuery(id+"F1.opExtrude","CAP_EDGE",EDGE,{"disambiguationData":[OSD([sQuery(id+"F0.wireOp",EDGE,"E3")])],"isStart":true}),"instanceName":"4"});
            var Q138;
            Q138=makeQuery(id+"F2.opPattern","COPY",EDGE,{"derivedFrom":makeQuery(id+"F1.opExtrude","CAP_EDGE",EDGE,{"disambiguationData":[OSD([sQuery(id+"F0.wireOp",EDGE,"E4")])],"isStart":true}),"instanceName":"4"});
            var Q139;
            Q139=makeQuery(id+"F2.opPattern","COPY",EDGE,{"derivedFrom":makeQuery(id+"F1.opExtrude","SWEPT_EDGE",EDGE,{"disambiguationData":[OSD([sQuery(id+"F0.wireOp",EDGE,"E3"),sQuery(id+"F0.wireOp",EDGE,"E4")])]}),"instanceName":"4"});
            var Q140;
            Q140=makeQuery(id+"F2.opPattern","COPY",EDGE,{"derivedFrom":makeQuery(id+"F1.opExtrude","CAP_EDGE",EDGE,{"disambiguationData":[OSD([sQuery(id+"F0.wireOp",EDGE,"E4")])],"isStart":false}),"instanceName":"4"});
            var Q141;
            Q141=makeQuery(id+"F2.opPattern","COPY",EDGE,{"derivedFrom":makeQuery(id+"F1.opExtrude","CAP_EDGE",EDGE,{"disambiguationData":[OSD([sQuery(id+"F0.wireOp",EDGE,"E4")])],"isStart":false}),"instanceName":"5"});
            var Q142;
            Q142=makeQuery(id+"F2.opPattern","COPY",FACE,{"derivedFrom":makeQuery(id+"F1.opExtrude","SWEPT_FACE",FACE,{"disambiguationData":[OSD([sQuery(id+"F0.wireOp",EDGE,"E5")])]}),"instanceName":"5"});
            var Q143;
            Q143=makeQuery(id+"F2.opPattern","COPY",EDGE,{"derivedFrom":makeQuery(id+"F1.opExtrude","CAP_EDGE",EDGE,{"disambiguationData":[OSD([sQuery(id+"F0.wireOp",EDGE,"E4")])],"isStart":true}),"instanceName":"5"});
            var Q144;
            Q144=makeQuery(id+"F2.opPattern","COPY",EDGE,{"derivedFrom":makeQuery(id+"F1.opExtrude","CAP_EDGE",EDGE,{"disambiguationData":[OSD([sQuery(id+"F0.wireOp",EDGE,"E4")])],"isStart":true}),"instanceName":"3"});
            var Q145;
            Q145=makeQuery(id+"F2.opPattern","COPY",EDGE,{"derivedFrom":makeQuery(id+"F1.opExtrude","CAP_EDGE",EDGE,{"disambiguationData":[OSD([sQuery(id+"F0.wireOp",EDGE,"E3")])],"isStart":false}),"instanceName":"3"});
            var Q146;
            Q146=makeQuery(id+"F2.opPattern","COPY",EDGE,{"derivedFrom":makeQuery(id+"F1.opExtrude","CAP_EDGE",EDGE,{"disambiguationData":[OSD([sQuery(id+"F0.wireOp",EDGE,"E3")])],"isStart":true}),"instanceName":"3"});
            var Q147;
            Q147=makeQuery(id+"F2.opPattern","COPY",EDGE,{"derivedFrom":makeQuery(id+"F1.opExtrude","CAP_EDGE",EDGE,{"disambiguationData":[OSD([sQuery(id+"F0.wireOp",EDGE,"E4")])],"isStart":false}),"instanceName":"3"});
            var Q148;
            Q148=makeQuery(id+"F2.opPattern","COPY",FACE,{"derivedFrom":makeQuery(id+"F1.opExtrude","SWEPT_FACE",FACE,{"disambiguationData":[OSD([sQuery(id+"F0.wireOp",EDGE,"E5")])]}),"instanceName":"3"});
            var Q149;
            Q149=makeQuery(id+"F2.opPattern","COPY",EDGE,{"derivedFrom":makeQuery(id+"F1.opExtrude","CAP_EDGE",EDGE,{"disambiguationData":[OSD([sQuery(id+"F0.wireOp",EDGE,"E2")])],"isStart":false}),"instanceName":"7"});
            var Q150;
            Q150=makeQuery(id+"F2.opPattern","COPY",FACE,{"derivedFrom":makeQuery(id+"F1.opExtrude","SWEPT_FACE",FACE,{"disambiguationData":[OSD([sQuery(id+"F0.wireOp",EDGE,"E5")])]}),"instanceName":"7"});
            var Q151;
            Q151=makeQuery(id+"F2.opPattern","COPY",EDGE,{"derivedFrom":makeQuery(id+"F1.opExtrude","SWEPT_EDGE",EDGE,{"disambiguationData":[OSD([sQuery(id+"F0.wireOp",EDGE,"E0"),sQuery(id+"F0.wireOp",EDGE,"E5")])]}),"instanceName":"7"});
            var Q152;
            Q152=makeQuery(id+"F2.opPattern","COPY",EDGE,{"derivedFrom":makeQuery(id+"F1.opExtrude","CAP_EDGE",EDGE,{"disambiguationData":[OSD([sQuery(id+"F0.wireOp",EDGE,"E3")])],"isStart":false}),"instanceName":"6"});
            var Q153;
            Q153=makeQuery(id+"F2.opPattern","COPY",EDGE,{"derivedFrom":makeQuery(id+"F1.opExtrude","CAP_EDGE",EDGE,{"disambiguationData":[OSD([sQuery(id+"F0.wireOp",EDGE,"E2")])],"isStart":true}),"instanceName":"6"});
            var Q154;
            Q154=makeQuery(id+"F2.opPattern","COPY",EDGE,{"derivedFrom":makeQuery(id+"F1.opExtrude","CAP_EDGE",EDGE,{"disambiguationData":[OSD([sQuery(id+"F0.wireOp",EDGE,"E4")])],"isStart":false}),"instanceName":"6"});
            var Q155;
            Q155=makeQuery(id+"F2.opPattern","COPY",EDGE,{"derivedFrom":makeQuery(id+"F1.opExtrude","CAP_EDGE",EDGE,{"disambiguationData":[OSD([sQuery(id+"F0.wireOp",EDGE,"E2")])],"isStart":false}),"instanceName":"6"});
            var Q156;
            Q156=makeQuery(id+"F2.opPattern","COPY",EDGE,{"derivedFrom":makeQuery(id+"F1.opExtrude","CAP_EDGE",EDGE,{"disambiguationData":[OSD([sQuery(id+"F0.wireOp",EDGE,"E3")])],"isStart":true}),"instanceName":"6"});
            var Q157;
            Q157=makeQuery(id+"F2.opPattern","COPY",EDGE,{"derivedFrom":makeQuery(id+"F1.opExtrude","CAP_EDGE",EDGE,{"disambiguationData":[OSD([sQuery(id+"F0.wireOp",EDGE,"E4")])],"isStart":true}),"instanceName":"6"});
            var Q158;
            Q158=makeQuery(id+"F2.opPattern","COPY",EDGE,{"derivedFrom":makeQuery(id+"F1.opExtrude","CAP_EDGE",EDGE,{"disambiguationData":[OSD([sQuery(id+"F0.wireOp",EDGE,"E5")])],"isStart":true}),"instanceName":"6"});
            var Q159;
            Q159=makeQuery(id+"F1.opExtrude","CAP_EDGE",EDGE,{"disambiguationData":[OSD([sQuery(id+"F0.wireOp",EDGE,"E2")])],"isStart":true});
            var Q160;
            Q160=makeQuery(id+"F1.opExtrude","CAP_EDGE",EDGE,{"disambiguationData":[OSD([sQuery(id+"F0.wireOp",EDGE,"E2")])],"isStart":false});
            var Q161;
            Q161=makeQuery(id+"F1.opExtrude","CAP_EDGE",EDGE,{"disambiguationData":[OSD([sQuery(id+"F0.wireOp",EDGE,"E4")])],"isStart":false});
            var Q162;
            Q162=makeQuery(id+"F1.opExtrude","CAP_EDGE",EDGE,{"disambiguationData":[OSD([sQuery(id+"F0.wireOp",EDGE,"E3")])],"isStart":false});
            var Q163;
            Q163=makeQuery(id+"F1.opExtrude","SWEPT_EDGE",EDGE,{"disambiguationData":[OSD([sQuery(id+"F0.wireOp",EDGE,"E0"),sQuery(id+"F0.wireOp",EDGE,"E5")])]});
            var Q164;
            Q164=makeQuery(id+"F1.opExtrude","SWEPT_FACE",FACE,{"disambiguationData":[OSD([sQuery(id+"F0.wireOp",EDGE,"E5")])]});
            var Q165;
            Q165=makeQuery(id+"F1.opExtrude","CAP_EDGE",EDGE,{"disambiguationData":[OSD([sQuery(id+"F0.wireOp",EDGE,"E4")])],"isStart":true});
            var Q166;
            Q166=makeQuery(id+"F1.opExtrude","CAP_EDGE",EDGE,{"disambiguationData":[OSD([sQuery(id+"F0.wireOp",EDGE,"E3")])],"isStart":true});
            var Q167;
            Q167=makeQuery(id+"F2.opPattern","COPY",EDGE,{"derivedFrom":makeQuery(id+"F1.opExtrude","SWEPT_EDGE",EDGE,{"disambiguationData":[OSD([sQuery(id+"F0.wireOp",EDGE,"E3"),sQuery(id+"F0.wireOp",EDGE,"E4")])]}),"instanceName":"2"});
            var Q168;
            Q168=makeQuery(id+"F2.opPattern","COPY",EDGE,{"derivedFrom":makeQuery(id+"F1.opExtrude","CAP_EDGE",EDGE,{"disambiguationData":[OSD([sQuery(id+"F0.wireOp",EDGE,"E4")])],"isStart":false}),"instanceName":"2"});
            var Q169;
            Q169=makeQuery(id+"F2.opPattern","COPY",FACE,{"derivedFrom":makeQuery(id+"F1.opExtrude","SWEPT_FACE",FACE,{"disambiguationData":[OSD([sQuery(id+"F0.wireOp",EDGE,"E3")])]}),"instanceName":"2"});
            var Q170;
            Q170=makeQuery(id+"F2.opPattern","COPY",EDGE,{"derivedFrom":makeQuery(id+"F1.opExtrude","SWEPT_EDGE",EDGE,{"disambiguationData":[OSD([sQuery(id+"F0.wireOp",EDGE,"E0"),sQuery(id+"F0.wireOp",EDGE,"E5")])]}),"instanceName":"2"});
            var Q171;
            Q171=makeQuery(id+"F2.opPattern","COPY",EDGE,{"derivedFrom":makeQuery(id+"F1.opExtrude","CAP_EDGE",EDGE,{"disambiguationData":[OSD([sQuery(id+"F0.wireOp",EDGE,"E2")])],"isStart":true}),"instanceName":"2"});
            var Q172;
            Q172=makeQuery(id+"F2.opPattern","COPY",EDGE,{"derivedFrom":makeQuery(id+"F1.opExtrude","CAP_EDGE",EDGE,{"disambiguationData":[OSD([sQuery(id+"F0.wireOp",EDGE,"E2")])],"isStart":false}),"instanceName":"2"});
            var Q173;
            Q173=makeQuery(id+"F2.opPattern","COPY",EDGE,{"derivedFrom":makeQuery(id+"F1.opExtrude","CAP_EDGE",EDGE,{"disambiguationData":[OSD([sQuery(id+"F0.wireOp",EDGE,"E4")])],"isStart":true}),"instanceName":"2"});
            var Q174;
            Q174=makeQuery(id+"F2.opPattern","COPY",EDGE,{"derivedFrom":makeQuery(id+"F1.opExtrude","CAP_EDGE",EDGE,{"disambiguationData":[OSD([sQuery(id+"F0.wireOp",EDGE,"E4")])],"isStart":true}),"instanceName":"1"});
            var Q175;
            Q175=makeQuery(id+"F2.opPattern","COPY",EDGE,{"derivedFrom":makeQuery(id+"F1.opExtrude","CAP_EDGE",EDGE,{"disambiguationData":[OSD([sQuery(id+"F0.wireOp",EDGE,"E5")])],"isStart":true}),"instanceName":"1"});
            var Q176;
            Q176=makeQuery(id+"F2.opPattern","COPY",EDGE,{"derivedFrom":makeQuery(id+"F1.opExtrude","CAP_EDGE",EDGE,{"disambiguationData":[OSD([sQuery(id+"F0.wireOp",EDGE,"E3")])],"isStart":false}),"instanceName":"1"});
            var Q177;
            Q177=makeQuery(id+"F2.opPattern","COPY",EDGE,{"derivedFrom":makeQuery(id+"F1.opExtrude","CAP_EDGE",EDGE,{"disambiguationData":[OSD([sQuery(id+"F0.wireOp",EDGE,"E4")])],"isStart":false}),"instanceName":"1"});
            var Q178;
            Q178=makeQuery(id+"F2.opPattern","COPY",EDGE,{"derivedFrom":makeQuery(id+"F1.opExtrude","CAP_EDGE",EDGE,{"disambiguationData":[OSD([sQuery(id+"F0.wireOp",EDGE,"E2")])],"isStart":false}),"instanceName":"1"});
            var Q179;
            Q179=makeQuery(id+"F2.opPattern","COPY",EDGE,{"derivedFrom":makeQuery(id+"F1.opExtrude","CAP_EDGE",EDGE,{"disambiguationData":[OSD([sQuery(id+"F0.wireOp",EDGE,"E3")])],"isStart":true}),"instanceName":"1"});
            var Q180;
            Q180=makeQuery(id+"F2.opPattern","COPY",EDGE,{"derivedFrom":makeQuery(id+"F1.opExtrude","CAP_EDGE",EDGE,{"disambiguationData":[OSD([sQuery(id+"F0.wireOp",EDGE,"E2")])],"isStart":true}),"instanceName":"1"});
            var Q181;
            Q181=makeQuery(id+"F2.opPattern","COPY",EDGE,{"derivedFrom":makeQuery(id+"F1.opExtrude","CAP_EDGE",EDGE,{"disambiguationData":[OSD([sQuery(id+"F0.wireOp",EDGE,"E5")])],"isStart":true}),"instanceName":"4"});
            var Q182;
            Q182=makeQuery(id+"F2.opPattern","COPY",EDGE,{"derivedFrom":makeQuery(id+"F1.opExtrude","CAP_EDGE",EDGE,{"disambiguationData":[OSD([sQuery(id+"F0.wireOp",EDGE,"E5")])],"isStart":true}),"instanceName":"5"});
            var Q183;
            Q183=makeQuery(id+"F2.opPattern","COPY",EDGE,{"derivedFrom":makeQuery(id+"F1.opExtrude","CAP_EDGE",EDGE,{"disambiguationData":[OSD([sQuery(id+"F0.wireOp",EDGE,"E5")])],"isStart":true}),"instanceName":"3"});
            var Q184;
            Q184=makeQuery(id+"F2.opPattern","COPY",EDGE,{"derivedFrom":makeQuery(id+"F1.opExtrude","SWEPT_EDGE",EDGE,{"disambiguationData":[OSD([sQuery(id+"F0.wireOp",EDGE,"E0"),sQuery(id+"F0.wireOp",EDGE,"E5")])]}),"instanceName":"3"});
            var Q185;
            Q185=makeQuery(id+"F2.opPattern","COPY",EDGE,{"derivedFrom":makeQuery(id+"F1.opExtrude","CAP_EDGE",EDGE,{"disambiguationData":[OSD([sQuery(id+"F0.wireOp",EDGE,"E5")])],"isStart":true}),"instanceName":"7"});
            var Q186;
            Q186=makeQuery(id+"F2.opPattern","COPY",EDGE,{"derivedFrom":makeQuery(id+"F1.opExtrude","SWEPT_EDGE",EDGE,{"disambiguationData":[OSD([sQuery(id+"F0.wireOp",EDGE,"E4"),sQuery(id+"F0.wireOp",EDGE,"E5")])]}),"instanceName":"7"});
            var Q187;
            Q187=makeQuery(id+"F2.opPattern","COPY",EDGE,{"derivedFrom":makeQuery(id+"F1.opExtrude","SWEPT_EDGE",EDGE,{"disambiguationData":[OSD([sQuery(id+"F0.wireOp",EDGE,"E0"),sQuery(id+"F0.wireOp",EDGE,"E5")])]}),"instanceName":"6"});
            var Q188;
            Q188=makeQuery(id+"F1.opExtrude","SWEPT_EDGE",EDGE,{"disambiguationData":[OSD([sQuery(id+"F0.wireOp",EDGE,"E4"),sQuery(id+"F0.wireOp",EDGE,"E5")])]});
            var Q189;
            Q189=makeQuery(id+"F1.opExtrude","CAP_EDGE",EDGE,{"disambiguationData":[OSD([sQuery(id+"F0.wireOp",EDGE,"E5")])],"isStart":false});
            var Q190;
            Q190=makeQuery(id+"F1.opExtrude","CAP_EDGE",EDGE,{"disambiguationData":[OSD([sQuery(id+"F0.wireOp",EDGE,"E5")])],"isStart":true});
            var Q191;
            Q191=makeQuery(id+"F2.opPattern","COPY",EDGE,{"derivedFrom":makeQuery(id+"F1.opExtrude","SWEPT_EDGE",EDGE,{"disambiguationData":[OSD([sQuery(id+"F0.wireOp",EDGE,"E4"),sQuery(id+"F0.wireOp",EDGE,"E5")])]}),"instanceName":"2"});
            var Q192;
            Q192=makeQuery(id+"F2.opPattern","COPY",EDGE,{"derivedFrom":makeQuery(id+"F1.opExtrude","CAP_EDGE",EDGE,{"disambiguationData":[OSD([sQuery(id+"F0.wireOp",EDGE,"E3")])],"isStart":true}),"instanceName":"2"});
            var Q193;
            Q193=makeQuery(id+"F2.opPattern","COPY",EDGE,{"derivedFrom":makeQuery(id+"F1.opExtrude","CAP_EDGE",EDGE,{"disambiguationData":[OSD([sQuery(id+"F0.wireOp",EDGE,"E5")])],"isStart":true}),"instanceName":"2"});
            var Q194;
            Q194=makeQuery(id+"F2.opPattern","COPY",EDGE,{"derivedFrom":makeQuery(id+"F1.opExtrude","CAP_EDGE",EDGE,{"disambiguationData":[OSD([sQuery(id+"F0.wireOp",EDGE,"E3")])],"isStart":false}),"instanceName":"2"});
            var Q195;
            Q195=makeQuery(id+"F2.opPattern","COPY",EDGE,{"derivedFrom":makeQuery(id+"F1.opExtrude","SWEPT_EDGE",EDGE,{"disambiguationData":[OSD([sQuery(id+"F0.wireOp",EDGE,"E4"),sQuery(id+"F0.wireOp",EDGE,"E5")])]}),"instanceName":"1"});
            var Q196;
            Q196=makeQuery(id+"F2.opPattern","COPY",EDGE,{"derivedFrom":makeQuery(id+"F1.opExtrude","SWEPT_EDGE",EDGE,{"disambiguationData":[OSD([sQuery(id+"F0.wireOp",EDGE,"E0"),sQuery(id+"F0.wireOp",EDGE,"E5")])]}),"instanceName":"5"});
            var Q197;
            Q197=makeQuery(id+"F2.opPattern","COPY",EDGE,{"derivedFrom":makeQuery(id+"F1.opExtrude","SWEPT_EDGE",EDGE,{"disambiguationData":[OSD([sQuery(id+"F0.wireOp",EDGE,"E4"),sQuery(id+"F0.wireOp",EDGE,"E5")])]}),"instanceName":"3"});
            var Q198;
            Q198=makeQuery(id+"F2.opPattern","COPY",EDGE,{"derivedFrom":makeQuery(id+"F1.opExtrude","SWEPT_EDGE",EDGE,{"disambiguationData":[OSD([sQuery(id+"F0.wireOp",EDGE,"E4"),sQuery(id+"F0.wireOp",EDGE,"E5")])]}),"instanceName":"6"});
            var Q199;
            Q199=makeQuery(id+"F2.opPattern","COPY",EDGE,{"derivedFrom":makeQuery(id+"F1.opExtrude","CAP_EDGE",EDGE,{"disambiguationData":[OSD([sQuery(id+"F0.wireOp",EDGE,"E5")])],"isStart":false}),"instanceName":"1"});
            var Q200;
            Q200=makeQuery(id+"F2.opPattern","COPY",EDGE,{"derivedFrom":makeQuery(id+"F1.opExtrude","CAP_EDGE",EDGE,{"disambiguationData":[OSD([sQuery(id+"F0.wireOp",EDGE,"E5")])],"isStart":false}),"instanceName":"2"});
            var Q201;
            Q201=makeQuery(id+"F2.opPattern","COPY",EDGE,{"derivedFrom":makeQuery(id+"F1.opExtrude","CAP_EDGE",EDGE,{"disambiguationData":[OSD([sQuery(id+"F0.wireOp",EDGE,"E5")])],"isStart":false}),"instanceName":"3"});
            var Q202;
            Q202=makeQuery(id+"F2.opPattern","COPY",EDGE,{"derivedFrom":makeQuery(id+"F1.opExtrude","CAP_EDGE",EDGE,{"disambiguationData":[OSD([sQuery(id+"F0.wireOp",EDGE,"E5")])],"isStart":false}),"instanceName":"4"});
            var Q203;
            Q203=makeQuery(id+"F2.opPattern","COPY",EDGE,{"derivedFrom":makeQuery(id+"F1.opExtrude","SWEPT_EDGE",EDGE,{"disambiguationData":[OSD([sQuery(id+"F0.wireOp",EDGE,"E4"),sQuery(id+"F0.wireOp",EDGE,"E5")])]}),"instanceName":"4"});
            var Q204;
            Q204=makeQuery(id+"F2.opPattern","COPY",EDGE,{"derivedFrom":makeQuery(id+"F1.opExtrude","CAP_EDGE",EDGE,{"disambiguationData":[OSD([sQuery(id+"F0.wireOp",EDGE,"E5")])],"isStart":false}),"instanceName":"5"});
            var Q205;
            Q205=makeQuery(id+"F2.opPattern","COPY",EDGE,{"derivedFrom":makeQuery(id+"F1.opExtrude","SWEPT_EDGE",EDGE,{"disambiguationData":[OSD([sQuery(id+"F0.wireOp",EDGE,"E4"),sQuery(id+"F0.wireOp",EDGE,"E5")])]}),"instanceName":"5"});
            var Q206;
            Q206=makeQuery(id+"F2.opPattern","COPY",EDGE,{"derivedFrom":makeQuery(id+"F1.opExtrude","CAP_EDGE",EDGE,{"disambiguationData":[OSD([sQuery(id+"F0.wireOp",EDGE,"E5")])],"isStart":false}),"instanceName":"6"});
            var Q207;
            Q207=makeQuery(id+"F2.opPattern","COPY",EDGE,{"derivedFrom":makeQuery(id+"F1.opExtrude","CAP_EDGE",EDGE,{"disambiguationData":[OSD([sQuery(id+"F0.wireOp",EDGE,"E5")])],"isStart":false}),"instanceName":"7"});
            fillet(context, id + "F3", {"entities" : qUnion([Q0, Q1, Q2, Q3, Q4, Q5, Q6, Q7, Q8, Q9, Q10, Q11, Q12, Q13, Q14, Q15, Q16, Q17, Q18, Q19, Q20, Q21, Q22, Q23, Q24, Q25, Q26, Q27, Q28, Q29, Q30, Q31, Q32, Q33, Q34, Q35, Q36, Q37, Q38, Q39, Q40, Q41, Q42, Q43, Q44, Q45, Q46, Q47, Q48, Q49, Q50, Q51, Q52, Q53, Q54, Q55, Q56, Q57, Q58, Q59, Q60, Q61, Q62, Q63, Q64, Q65, Q66, Q67, Q68, Q69, Q70, Q71, Q72, Q73, Q74, Q75, Q76, Q77, Q78, Q79, Q80, Q81, Q82, Q83, Q84, Q85, Q86, Q87, Q88, Q89, Q90, Q91, Q92, Q93, Q94, Q95, Q96, Q97, Q98, Q99, Q100, Q101, Q102, Q103, Q104, Q105, Q106, Q107, Q108, Q109, Q110, Q111, Q112, Q113, Q114, Q115, Q116, Q117, Q118, Q119, Q120, Q121, Q122, Q123, Q124, Q125, Q126, Q127, Q128, Q129, Q130, Q131, Q132, Q133, Q134, Q135, Q136, Q137, Q138, Q139, Q140, Q141, Q142, Q143, Q144, Q145, Q146, Q147, Q148, Q149, Q150, Q151, Q152, Q153, Q154, Q155, Q156, Q157, Q158, Q159, Q160, Q161, Q162, Q163, Q164, Q165, Q166, Q167, Q168, Q169, Q170, Q171, Q172, Q173, Q174, Q175, Q176, Q177, Q178, Q179, Q180, Q181, Q182, Q183, Q184, Q185, Q186, Q187, Q188, Q189, Q190, Q191, Q192, Q193, Q194, Q195, Q196, Q197, Q198, Q199, Q200, Q201, Q202, Q203, Q204, Q205, Q206, Q207]), "radius" : .1 * mm, "tangentPropagation" : true, "allowEdgeOverflow" : false});
        }
    });
